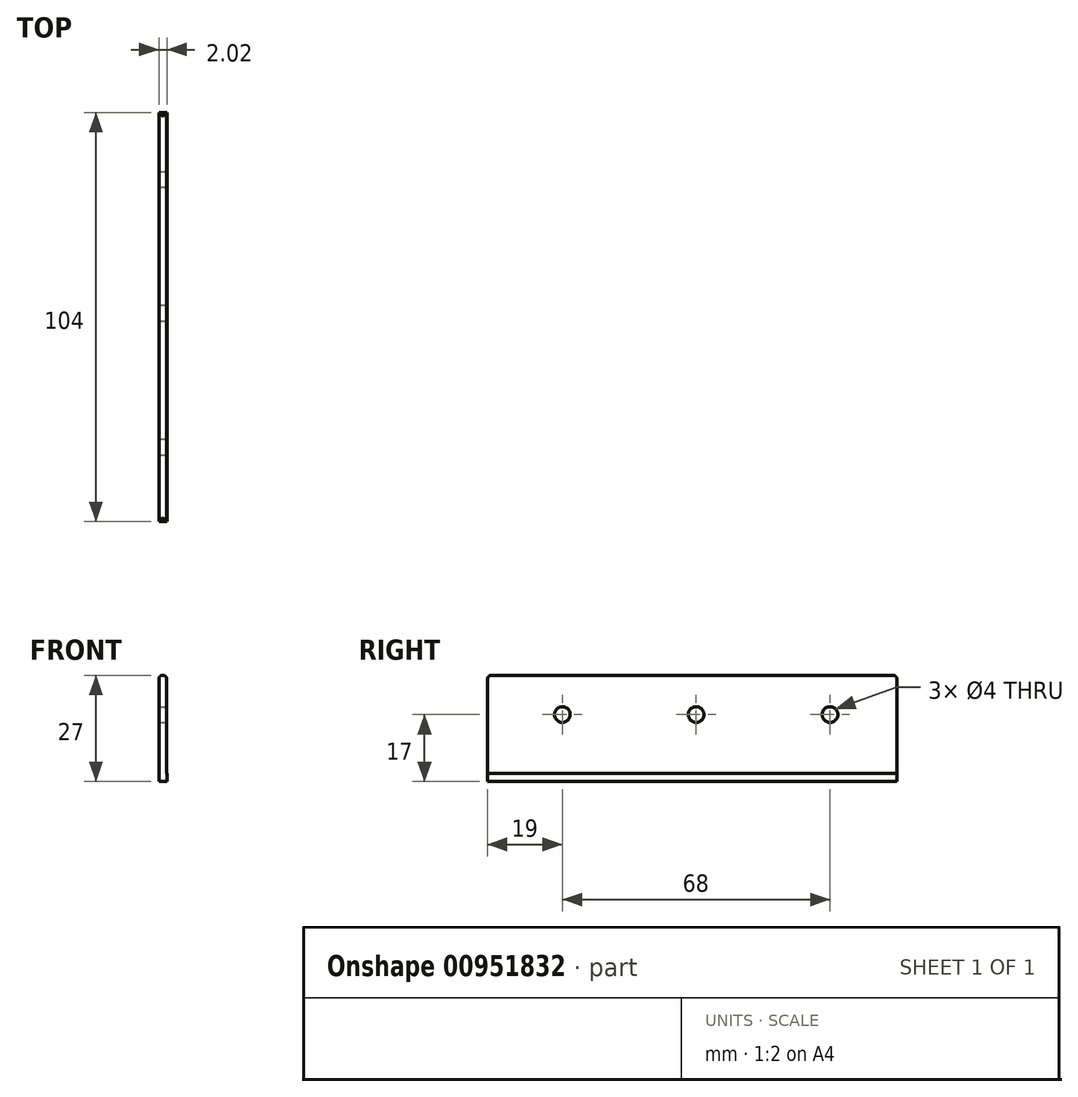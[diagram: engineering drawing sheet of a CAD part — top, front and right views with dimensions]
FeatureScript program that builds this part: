
annotation { "Feature Type Name" : "Feature", "Feature Type Description" : "" }
export const myFeature = defineFeature(function(context is Context, id is Id, definition is map)
    precondition{}
    {
        {
            var Q0;
            Q0=qCreatedBy(makeId("Top.planeOp"),FACE);
            var sketch = newSketch(context, id + "F0", { "sketchPlane" : qUnion([Q0])});
            skLineSegment(sketch, "E0.bottom", {"start": v(-52, 52) * mm, "end": v(52, 52) * mm});
            skLineSegment(sketch, "E0.top", {"start": v(-52, -52) * mm, "end": v(52, -52) * mm});
            skLineSegment(sketch, "E0.left", {"start": v(-52, 52) * mm, "end": v(-52, -52) * mm});
            skLineSegment(sketch, "E0.right", {"start": v(52, 52) * mm, "end": v(52, -52) * mm});
            skPoint(sketch, "E0.middle", {"position": v(0, 0) * mm});
            skSolve(sketch);
        }
        {
            var Q0;
            Q0=qSketchRegion(id+"F0",true);
            extrude(context, id + "F1", {"entities" : qUnion([Q0]), "depth" : 2 * mm, "offsetDistance" : 25 * mm});
        }
        {
            var Q0;
            Q0=makeQuery(id+"F1.opExtrude","CAP_FACE",FACE,{"disambiguationData":[OSD([sQuery(id+"F0.wireOp",EDGE,"E0.bottom"),sQuery(id+"F0.wireOp",EDGE,"E0.top"),sQuery(id+"F0.wireOp",EDGE,"E0.left"),sQuery(id+"F0.wireOp",EDGE,"E0.right")])],"isStart":false});
            var sketch = newSketch(context, id + "F2", { "sketchPlane" : qUnion([Q0])});
            skLineSegment(sketch, "E1.bottom", {"start": v(-52, 52) * mm, "end": v(-50, 52) * mm});
            skLineSegment(sketch, "E1.top", {"start": v(-52, -52) * mm, "end": v(-50, -52) * mm});
            skLineSegment(sketch, "E1.left", {"start": v(-52, 52) * mm, "end": v(-52, -52) * mm});
            skLineSegment(sketch, "E1.right", {"start": v(-50, 52) * mm, "end": v(-50, -52) * mm});
            skSolve(sketch);
        }
        {
            var Q0;
            Q0=qSketchRegion(id+"F2",true);
            extrude(context, id + "F3", {"entities" : qUnion([Q0]), "operationType" : NewBodyOperationType.ADD, "depth" : 25 * mm, "offsetDistance" : 25 * mm});
        }
        {
            var Q0;
            Q0=makeQuery(id+"F1.opExtrude","CAP_FACE",FACE,{"disambiguationData":[OSD([sQuery(id+"F0.wireOp",EDGE,"E0.bottom"),sQuery(id+"F0.wireOp",EDGE,"E0.top"),sQuery(id+"F0.wireOp",EDGE,"E0.left"),sQuery(id+"F0.wireOp",EDGE,"E0.right")])],"isStart":false});
            var sketch = newSketch(context, id + "F4", { "sketchPlane" : qUnion([Q0])});
            skLineSegment(sketch, "E2.bottom", {"start": v(52, 52) * mm, "end": v(50, 52) * mm});
            skLineSegment(sketch, "E2.top", {"start": v(52, -52) * mm, "end": v(50, -52) * mm});
            skLineSegment(sketch, "E2.left", {"start": v(52, 52) * mm, "end": v(52, -52) * mm});
            skLineSegment(sketch, "E2.right", {"start": v(50, 52) * mm, "end": v(50, -52) * mm});
            skSolve(sketch);
        }
        {
            var Q0;
            Q0=qSketchRegion(id+"F4",true);
            extrude(context, id + "F5", {"entities" : qUnion([Q0]), "operationType" : NewBodyOperationType.ADD, "depth" : 25 * mm, "offsetDistance" : 25 * mm});
        }
        {
            var Q0;
            Q0=makeQuery(id+"F5.opExtrude","CAP_FACE",FACE,{"disambiguationData":[OSD([sQuery(id+"F4.wireOp",EDGE,"E2.bottom"),sQuery(id+"F4.wireOp",EDGE,"E2.top"),sQuery(id+"F4.wireOp",EDGE,"E2.left"),sQuery(id+"F4.wireOp",EDGE,"E2.right")])],"isStart":false});
            fillet(context, id + "F6", {"entities" : qUnion([Q0]), "radius" : 1 * mm, "tangentPropagation" : true, "allowEdgeOverflow" : false});
        }
        {
            var Q0;
            Q0=makeQuery(id+"F3.opExtrude","CAP_FACE",FACE,{"disambiguationData":[OSD([sQuery(id+"F2.wireOp",EDGE,"E1.bottom"),sQuery(id+"F2.wireOp",EDGE,"E1.top"),sQuery(id+"F2.wireOp",EDGE,"E1.left"),sQuery(id+"F2.wireOp",EDGE,"E1.right")])],"isStart":false});
            fillet(context, id + "F7", {"entities" : qUnion([Q0]), "radius" : 1 * mm, "tangentPropagation" : true, "allowEdgeOverflow" : false});
        }
        {
            var Q0;
            Q0=makeQuery(id+"F5.boolean.opBoolean","MERGE",FACE,{"derivedFrom":[makeQuery(id+"F1.opExtrude","SWEPT_FACE",FACE,{"disambiguationData":[OSD([sQuery(id+"F0.wireOp",EDGE,"E0.right")])]}),makeQuery(id+"F5.opExtrude","SWEPT_FACE",FACE,{"disambiguationData":[OSD([sQuery(id+"F4.wireOp",EDGE,"E2.left")])]})]});
            var sketch = newSketch(context, id + "F8", { "sketchPlane" : qUnion([Q0])});
            skCircle(sketch, "E3", {"center": v(-33, 17) * mm, "radius": 2.83 * mm});
            skSolve(sketch);
        }
        {
            var Q0;
            Q0=sQuery(id+"F8.wireOp",VERTEX,"E3.center");
            var Q1;
            Q1=makeQuery(id+"F1.opExtrude","SWEPT_BODY",BODY,{"disambiguationData":[OSD([sQuery(id+"F0.wireOp",EDGE,"E0.bottom"),sQuery(id+"F0.wireOp",EDGE,"E0.top"),sQuery(id+"F0.wireOp",EDGE,"E0.left"),sQuery(id+"F0.wireOp",EDGE,"E0.right")])]});
            hole(context, id + "F9", {"style" : HoleStyle.SIMPLE, "endStyle" : HoleEndStyle.THROUGH, "holeDiameter" : 4 * mm, "majorDiameter" : 5 * mm, "isTappedThrough" : true, "tappedDepth" : 12 * mm, "tapClearance" : 3, "locations" : qUnion([Q0]), "scope" : qUnion([Q1])});
        }
        {
            var Q0;
            Q0=makeQuery(id+"F5.boolean.opBoolean","MERGE",FACE,{"derivedFrom":[makeQuery(id+"F1.opExtrude","SWEPT_FACE",FACE,{"disambiguationData":[OSD([sQuery(id+"F0.wireOp",EDGE,"E0.right")])]}),makeQuery(id+"F5.opExtrude","SWEPT_FACE",FACE,{"disambiguationData":[OSD([sQuery(id+"F4.wireOp",EDGE,"E2.left")])]})]});
            var sketch = newSketch(context, id + "F10", { "sketchPlane" : qUnion([Q0])});
            skCircle(sketch, "E4", {"center": v(1, 17) * mm, "radius": 2 * mm});
            skSolve(sketch);
        }
        {
            var Q0;
            Q0=sQuery(id+"F10.wireOp",VERTEX,"E4.center");
            var Q1;
            Q1=makeQuery(id+"F1.opExtrude","SWEPT_BODY",BODY,{"disambiguationData":[OSD([sQuery(id+"F0.wireOp",EDGE,"E0.bottom"),sQuery(id+"F0.wireOp",EDGE,"E0.top"),sQuery(id+"F0.wireOp",EDGE,"E0.left"),sQuery(id+"F0.wireOp",EDGE,"E0.right")])]});
            hole(context, id + "F11", {"style" : HoleStyle.SIMPLE, "endStyle" : HoleEndStyle.THROUGH, "holeDiameter" : 4 * mm, "majorDiameter" : 5 * mm, "isTappedThrough" : true, "tappedDepth" : 12 * mm, "tapClearance" : 3, "locations" : qUnion([Q0]), "scope" : qUnion([Q1])});
        }
        {
            var Q0;
            Q0=makeQuery(id+"F5.boolean.opBoolean","MERGE",FACE,{"derivedFrom":[makeQuery(id+"F1.opExtrude","SWEPT_FACE",FACE,{"disambiguationData":[OSD([sQuery(id+"F0.wireOp",EDGE,"E0.right")])]}),makeQuery(id+"F5.opExtrude","SWEPT_FACE",FACE,{"disambiguationData":[OSD([sQuery(id+"F4.wireOp",EDGE,"E2.left")])]})]});
            var sketch = newSketch(context, id + "F12", { "sketchPlane" : qUnion([Q0])});
            skCircle(sketch, "E5", {"center": v(35, 17) * mm, "radius": 2 * mm});
            skSolve(sketch);
        }
        {
            var Q0;
            Q0=sQuery(id+"F12.wireOp",VERTEX,"E5.center");
            var Q1;
            Q1=makeQuery(id+"F1.opExtrude","SWEPT_BODY",BODY,{"disambiguationData":[OSD([sQuery(id+"F0.wireOp",EDGE,"E0.bottom"),sQuery(id+"F0.wireOp",EDGE,"E0.top"),sQuery(id+"F0.wireOp",EDGE,"E0.left"),sQuery(id+"F0.wireOp",EDGE,"E0.right")])]});
            hole(context, id + "F13", {"style" : HoleStyle.SIMPLE, "endStyle" : HoleEndStyle.THROUGH, "holeDiameter" : 4 * mm, "majorDiameter" : 5 * mm, "isTappedThrough" : true, "tappedDepth" : 12 * mm, "tapClearance" : 3, "locations" : qUnion([Q0]), "scope" : qUnion([Q1])});
        }
        {
            var Q0;
            Q0=qCreatedBy(makeId("Front.planeOp"),FACE);
            var sketch = newSketch(context, id + "F14", { "sketchPlane" : qUnion([Q0])});
            skLineSegment(sketch, "E6", {"start": v(-49.98, 2.72) * mm, "end": v(-49.98, 0) * mm});
            skLineSegment(sketch, "E7", {"start": v(-49.98, 0) * mm, "end": v(-49.98, -1.5) * mm});
            skLineSegment(sketch, "E8", {"start": v(-49.98, -1.5) * mm, "end": v(74.38, -1.5) * mm});
            skLineSegment(sketch, "E9", {"start": v(74.38, -1.5) * mm, "end": v(74.38, 39.03) * mm});
            skLineSegment(sketch, "E10", {"start": v(74.38, 39.03) * mm, "end": v(-49.98, 2.72) * mm});
            skSolve(sketch);
        }
        {
            var Q0;
            Q0 = qSketchRegion(id + "F14", true);
            extrude(context, id + "F15", {"entities" : qUnion([Q0]), "operationType" : NewBodyOperationType.REMOVE, "depth" : 500 * mm, "offsetDistance" : 25 * mm});
        }
        {
            var Q0;
            Q0 = qSketchRegion(id + "F14", true);
            extrude(context, id + "F16", {"entities" : qUnion([Q0]), "operationType" : NewBodyOperationType.REMOVE, "oppositeDirection" : true, "depth" : 505 * mm, "offsetDistance" : 25 * mm});
        }
    });
